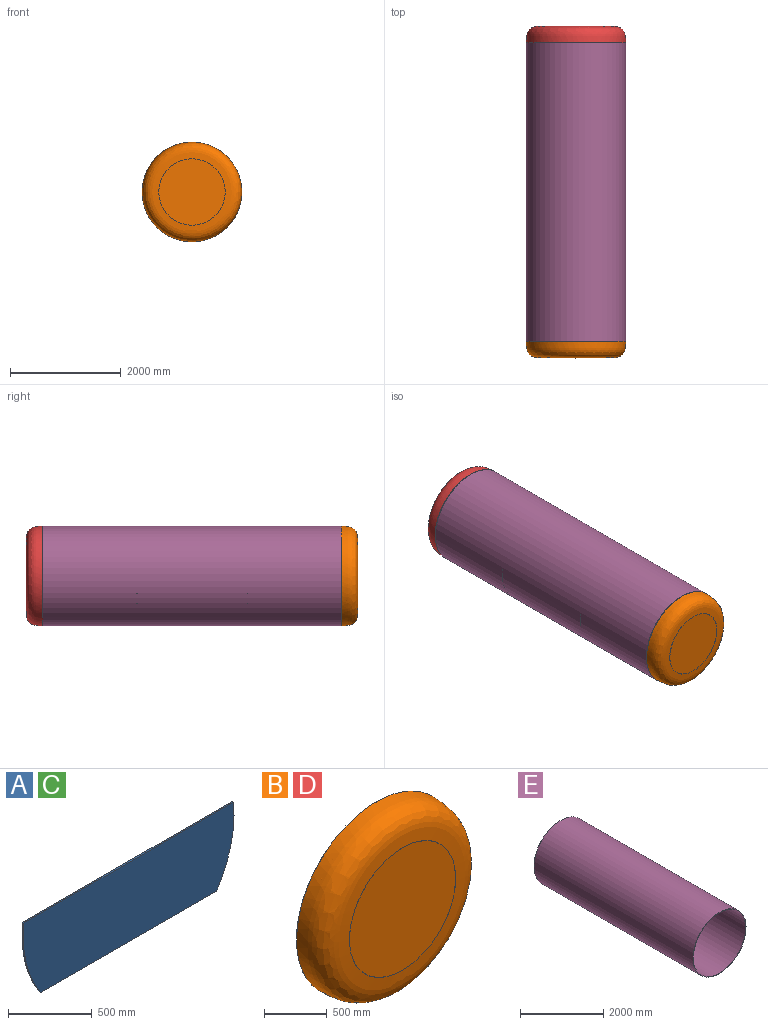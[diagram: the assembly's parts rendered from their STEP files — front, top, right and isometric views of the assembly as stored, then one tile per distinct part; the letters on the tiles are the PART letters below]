
ASSEMBLY  parts=5 mates=4
PART A: 6 faces, bbox 1780x10x580 mm
  f0: plane 1770.88x10mm, normal (0,0,1), area 17708.8mm2, adj f1,f3,f4,f5
  f1: cylinder r=890mm len=580mm, axis (0,1,0), area 6090.6mm2, adj f0,f2,f4,f5
  f2: plane 1485.93x10mm, normal (0,0,-1), area 14859.3mm2, adj f1,f3,f4,f5
  f3: cylinder r=890mm len=580mm, axis (0,1,0), area 6090.6mm2, adj f0,f2,f4,f5
  f4: plane 1780x580mm, normal (0,-1,0), area 985804mm2, adj f0,f1,f2,f3
  f5: plane 1780x580mm, normal (0,1,0), area 985804mm2, adj f0,f1,f2,f3
PART B: 5 faces, bbox 1805x305x1805 mm
  f0: plane 1200.03x1200.03mm, normal (0,-1,0), area 1130975.1mm2, adj f2
  f1: plane 1802.1x1802.1mm, normal (0,1,0), area 14235.7mm2, adj f2,f4
  f2: bspline ~1800x1800mm, area 2562303.7mm2, adj f0,f1
  f3: plane 1200x1200mm, normal (0,1,0), area 1130975.1mm2, adj f4
  f4: offset ~1805x1805mm, area 2537370.3mm2, adj f1,f3
PART C: same geometry as A
PART D: same geometry as B
PART E: 4 faces, bbox 1800x5400x1800 mm
  f0: cylinder r=890mm len=5400mm, axis (0,1,0), area 30196988.6mm2, adj f2,f3
  f1: cylinder r=900mm len=5400mm, axis (0,1,0), area 30536280.6mm2, adj f2,f3
  f2: plane 1800x1800mm, normal (0,-1,0), area 56234.5mm2, adj f0,f1
  f3: plane 1800x1800mm, normal (0,1,0), area 56234.5mm2, adj f0,f1
PLACE A t=(819.94,-5999.8,93.59)mm
PLACE B t=(633.57,-7699.8,212.16)mm
PLACE C t=(819.94,-3999.8,93.59)mm
PLACE D rot(axis=(0,0,1),180deg) t=(225.09,-2299.8,212.16)mm
PLACE E t=(533.39,-2299.8,281.77)mm
MATE fastened C.f1 <-> E.f0  axis (0,-1,0) through (429.33,-3999.8,321.95)mm
MATE fastened E.f0 <-> B.f1  axis (0,-1,0) through (429.33,-7699.8,321.95)mm
MATE fastened A.f1 <-> E.f0  axis (0,-1,0) through (429.33,-5999.8,321.95)mm
MATE fastened D.f1 <-> E.f0  axis (0,-1,0) through (429.33,-2299.8,321.95)mm
